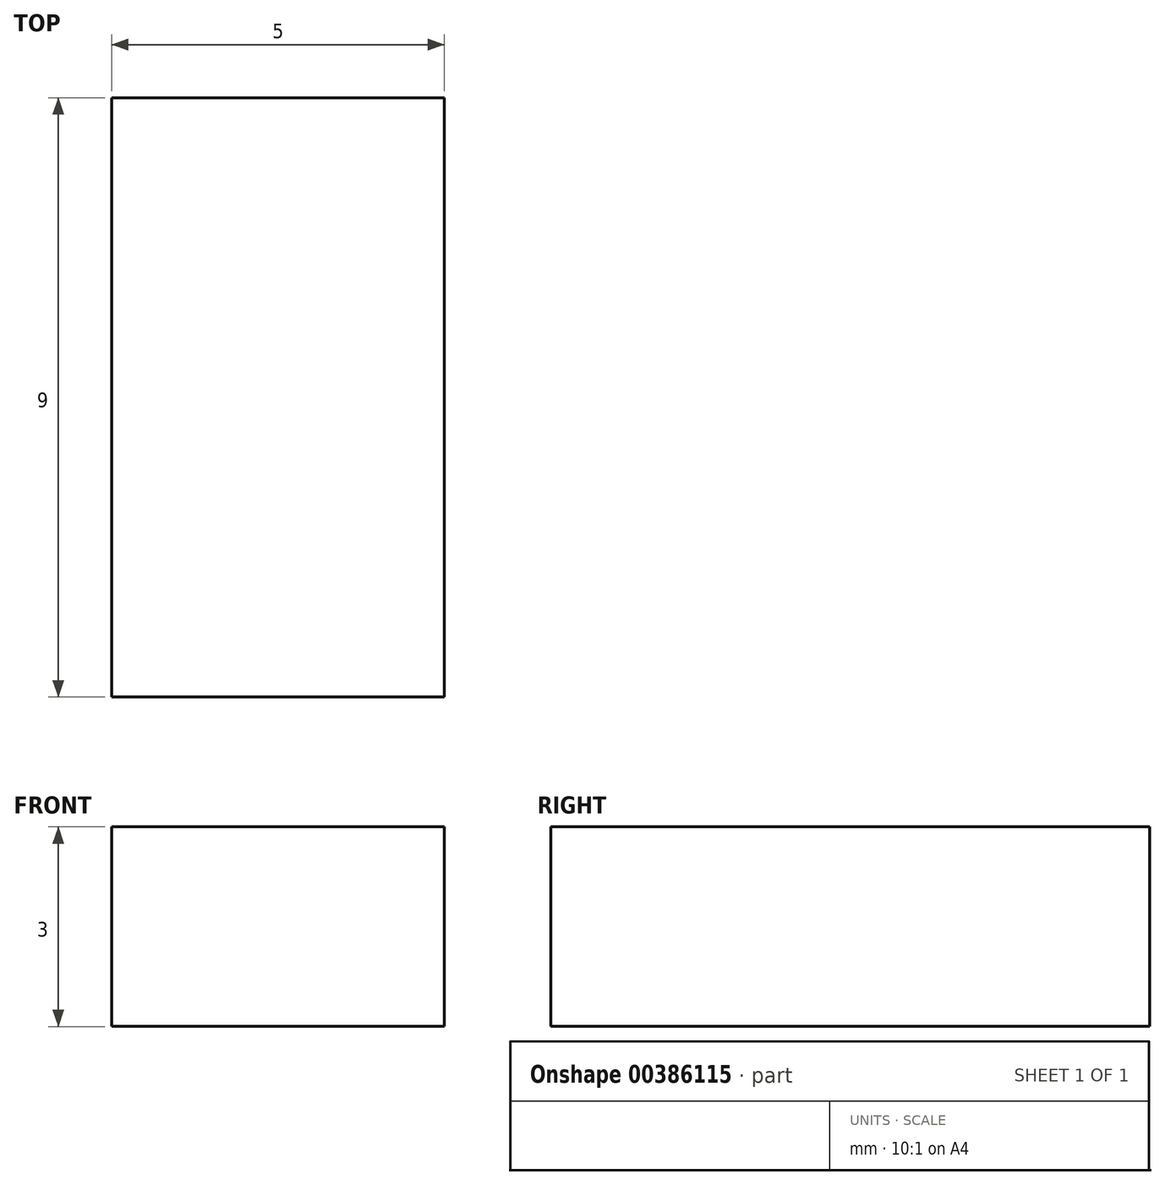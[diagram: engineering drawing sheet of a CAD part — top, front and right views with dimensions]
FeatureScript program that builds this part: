
annotation { "Feature Type Name" : "Feature", "Feature Type Description" : "" }
export const myFeature = defineFeature(function(context is Context, id is Id, definition is map)
    precondition{}
    {
        {
            var Q0;
            Q0=qCreatedBy(makeId("Front.planeOp"),FACE);
            var sketch = newSketch(context, id + "F0", { "sketchPlane" : qUnion([Q0])});
            skLineSegment(sketch, "E0.bottom", {"start": v(-5, -14.03) * mm, "end": v(0, -14.03) * mm});
            skLineSegment(sketch, "E0.top", {"start": v(-5, -11.03) * mm, "end": v(0, -11.03) * mm});
            skLineSegment(sketch, "E0.left", {"start": v(-5, -14.03) * mm, "end": v(-5, -11.03) * mm});
            skLineSegment(sketch, "E0.right", {"start": v(0, -14.03) * mm, "end": v(0, -11.03) * mm});
            skSolve(sketch);
        }
        {
            var Q0;
            Q0=makeQuery(id+"F0.imprint","IMPRINT",FACE,{"disambiguationData":[TD([[makeQuery(id+"F0.imprint","IMPRINT",EDGE,{"derivedFrom":sQuery(id+"F0.wireOp",EDGE,"E0.bottom")}),1.0]])]});
            extrude(context, id + "F1", {"entities" : qUnion([Q0]), "depth" : 9 * mm});
        }
    });
